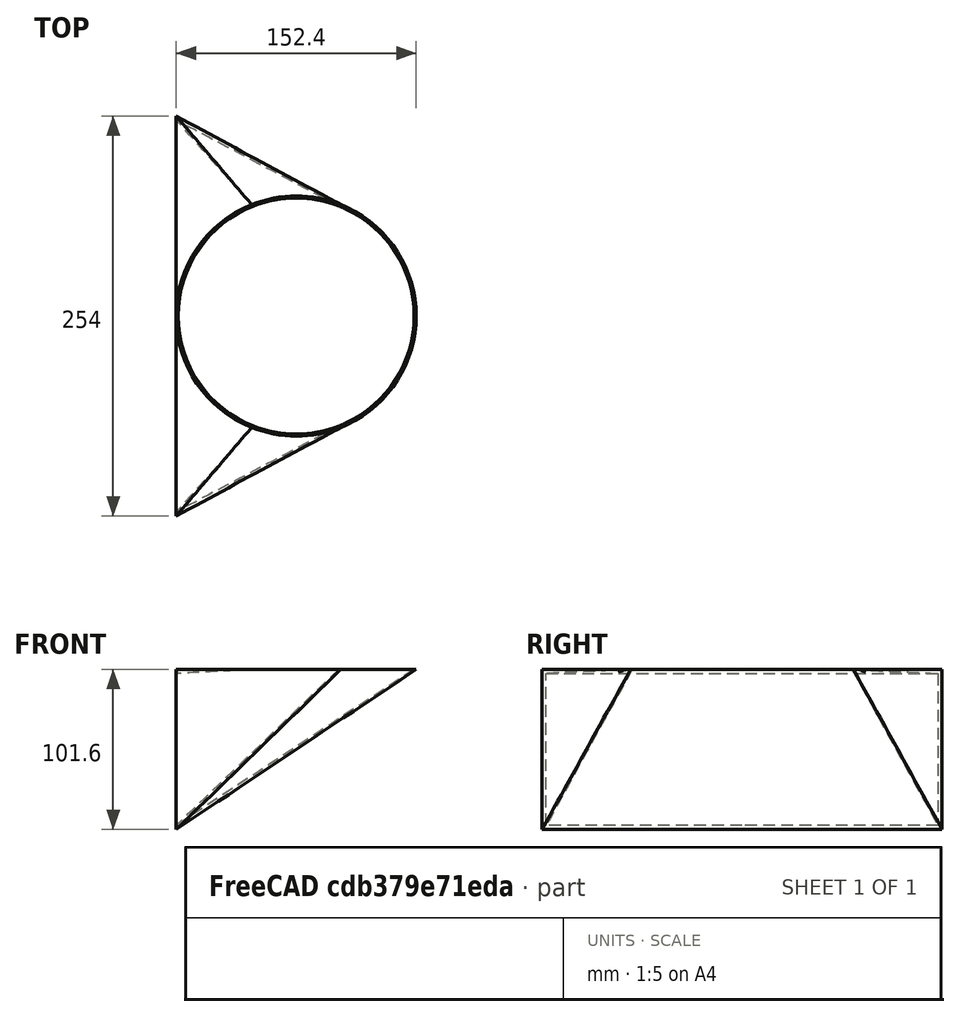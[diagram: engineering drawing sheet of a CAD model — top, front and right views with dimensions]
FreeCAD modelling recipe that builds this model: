
FCSTD DOCUMENT  (FreeCAD 0.21R33694 (Git))
Label: 90deg-register-box
License: All rights reserved
LicenseURL: http://en.wikipedia.org/wiki/All_rights_reserved
objects: Sketcher::SketchObject×2, PartDesign::AdditiveLoft×1, PartDesign::Body×1
note: 5 computed .brp shape members not serialized (recipe doc carries the construction recipe); baked Part::Feature solids carry a one-line shape summary decoded from their .brp

FEATURE [Sketcher::SketchObject] Sketch
  FullyConstrained = true
  MapMode = 5
  Placement = pos=(0,0,0) rot=(0.57735,0.57735,0.57735;2.0944rad)
  Support = -> [YZ_Plane]
  sketch-geometry (8):
    g0: LineSegment StartX=-127 StartY=50.8 StartZ=0 EndX=127 EndY=50.8 EndZ=0
    g1: LineSegment StartX=127 StartY=50.8 StartZ=0 EndX=127 EndY=-50.8 EndZ=0
    g2: LineSegment StartX=127 StartY=-50.8 StartZ=0 EndX=-127 EndY=-50.8 EndZ=0
    g3: LineSegment StartX=-127 StartY=-50.8 StartZ=0 EndX=-127 EndY=50.8 EndZ=0
    g4: LineSegment StartX=-124.46 StartY=48.26 StartZ=0 EndX=124.46 EndY=48.26 EndZ=0
    g5: LineSegment StartX=124.46 StartY=48.26 StartZ=0 EndX=124.46 EndY=-48.26 EndZ=0
    g6: LineSegment StartX=124.46 StartY=-48.26 StartZ=0 EndX=-124.46 EndY=-48.26 EndZ=0
    g7: LineSegment StartX=-124.46 StartY=-48.26 StartZ=0 EndX=-124.46 EndY=48.26 EndZ=0
  constraints (20):
    c: Coincident(g0,g1)
    c: Coincident(g1,g2)
    c: Coincident(g2,g3)
    c: Coincident(g3,g0)
    c: Horizontal(g0)
    c: Vertical(g3)
    c: Symmetric(g1,g2,g-2)
    c: Symmetric(g0,g1,g-1)
    c: DistanceY(g3,g3) = 101.6
    c: DistanceX(g0,g0) = 254
    c: Coincident(g4,g5)
    c: Coincident(g5,g6)
    c: Coincident(g6,g7)
    c: Coincident(g7,g4)
    c: Horizontal(g6)
    c: Vertical(g5)
    c: Symmetric(g4,g6,g-1)
    c: Symmetric(g4,g4,g-2)
    c: DistanceX(g0,g4) = 2.54
    c: DistanceY(g4,g0) = 2.54
FEATURE [Sketcher::SketchObject] Sketch001
  FullyConstrained = true
  MapMode = 5
  Placement = pos=(0,0,50.8) rot=(1,0,0;3.14159rad)
  sketch-geometry (2):
    g0: Circle CenterX=76.2 CenterY=0 CenterZ=0 NormalX=0 NormalY=0 NormalZ=1 AngleXU=0 Radius=76.2
    g1: Circle CenterX=76.2 CenterY=0 CenterZ=0 NormalX=0 NormalY=0 NormalZ=1 AngleXU=0 Radius=74.93
  constraints (5):
    c: PointOnObject(g0,g-1)
    c: Diameter(g0) = 152.4
    c: Tangent(g0,g-2)
    c: Coincident(g1,g0)
    c: Diameter(g1) = 149.86
FEATURE [PartDesign::AdditiveLoft] AdditiveLoft
  Closed = false
  Placement = pos=(0,0,50.8) rot=(1,0,0;3.14159rad)
  Profile = -> Sketch001
  Ruled = false
  Sections = -> [Sketch]
FEATURE [PartDesign::Body] Body
  Group = -> [Sketch,Sketch001,AdditiveLoft]
  Origin = -> Origin
  Tip = -> AdditiveLoft
